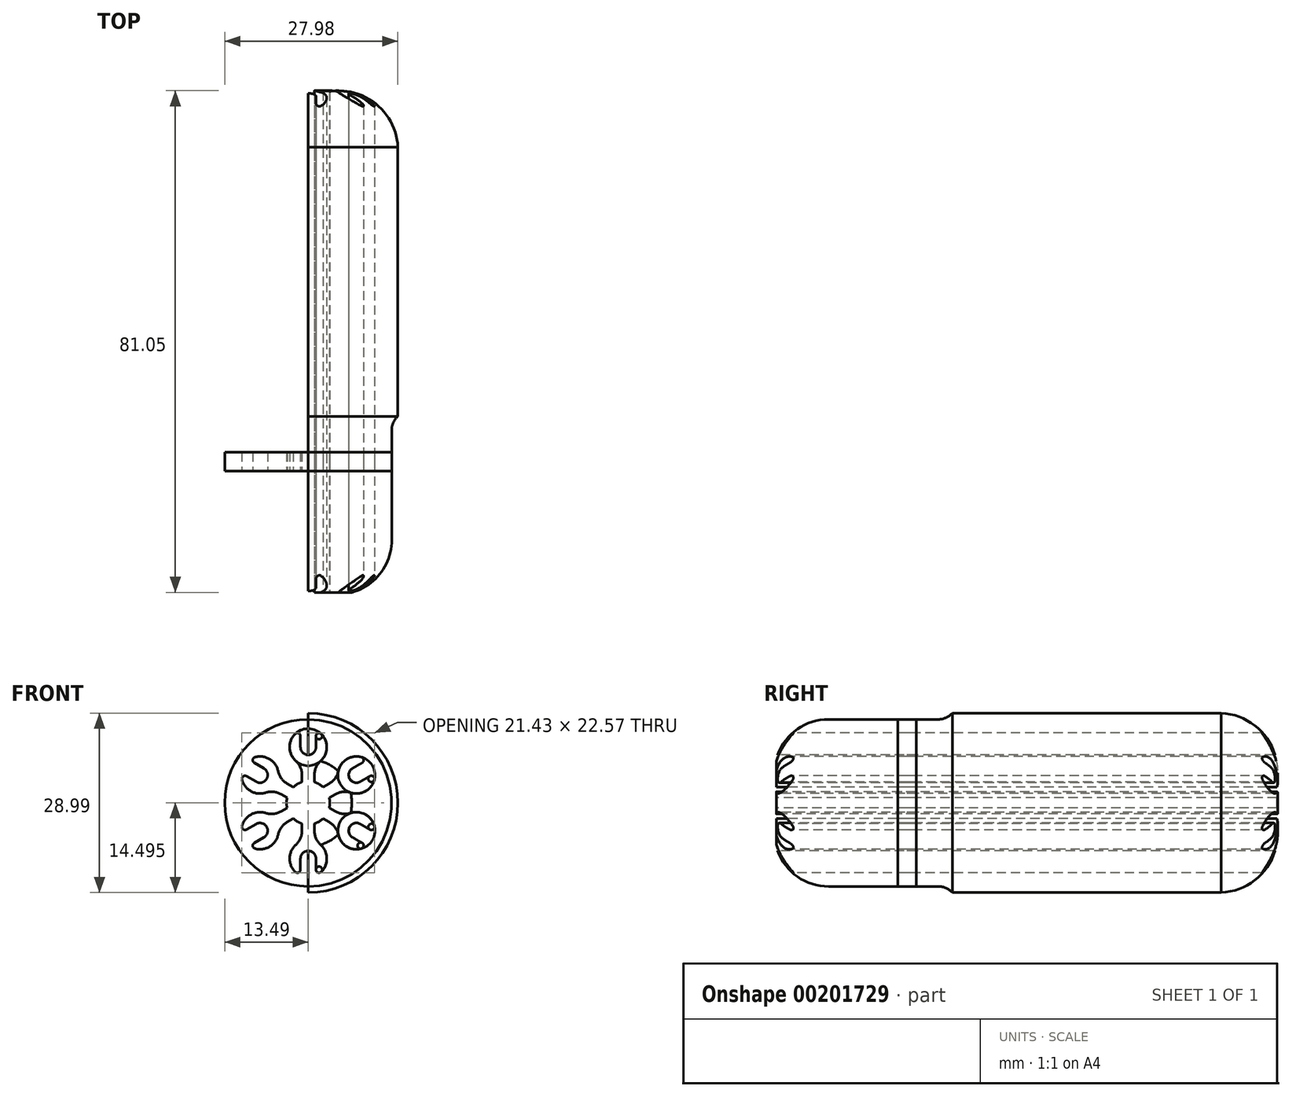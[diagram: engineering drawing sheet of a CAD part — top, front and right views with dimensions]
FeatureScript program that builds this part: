
annotation { "Feature Type Name" : "Feature", "Feature Type Description" : "" }
export const myFeature = defineFeature(function(context is Context, id is Id, definition is map)
    precondition{}
    {
        {
            var Q0;
            Q0=qCreatedBy(makeId("Right.planeOp"),FACE);
            var sketch = newSketch(context, id + "F0", { "sketchPlane" : qUnion([Q0])});
            skLineSegment(sketch, "E0.bottom", {"start": v(-3.13, 33.38) * mm, "end": v(86.87, 33.38) * mm});
            skLineSegment(sketch, "E0.top", {"start": v(-3.13, 32.38) * mm, "end": v(4.08, 32.38) * mm});
            skLineSegment(sketch, "E0.left", {"start": v(-3.13, 33.38) * mm, "end": v(-3.13, 32.38) * mm});
            skLineSegment(sketch, "E0.right", {"start": v(86.87, 33.38) * mm, "end": v(86.87, 32.38) * mm});
            skPoint(sketch, "E0.middle", {"position": v(41.87, 32.88) * mm});
            skLineSegment(sketch, "E1.bottom", {"start": v(86.87, 32.38) * mm, "end": v(81.87, 32.38) * mm, "construction": true});
            skLineSegment(sketch, "E1.top", {"start": v(86.87, 21.38) * mm, "end": v(85.87, 21.38) * mm});
            skLineSegment(sketch, "E1.left", {"start": v(86.87, 32.38) * mm, "end": v(86.87, 21.38) * mm, "construction": true});
            skLineSegment(sketch, "E1.right", {"start": v(81.87, 32.38) * mm, "end": v(81.87, 21.38) * mm, "construction": true});
            skLineSegment(sketch, "E2.bottom", {"start": v(81.87, 32.38) * mm, "end": v(71.87, 32.38) * mm, "construction": true});
            skLineSegment(sketch, "E2.top", {"start": v(81.87, 21.38) * mm, "end": v(71.87, 21.38) * mm, "construction": true});
            skLineSegment(sketch, "E2.right", {"start": v(71.87, 33.38) * mm, "end": v(71.87, 21.38) * mm, "construction": true});
            skLineSegment(sketch, "E3.0", {"start": v(85.87, 22.38) * mm, "end": v(85.37, 22.38) * mm, "construction": true});
            skLineSegment(sketch, "E4.0", {"start": v(85.87, 32.38) * mm, "end": v(85.87, 21.38) * mm, "construction": true});
            skArc(sketch, "E5", {"start": v(82.3, 22.38) * mm, "mid": v(80.84, 28.3) * mm, "end": v(76.33, 32.38) * mm});
            skArc(sketch, "E6", {"start": v(81.87, 21.38) * mm, "mid": v(79.3, 29.1) * mm, "end": v(71.87, 32.38) * mm});
            skLineSegment(sketch, "E7.trimOffspring", {"start": v(76.33, 32.38) * mm, "end": v(86.87, 32.38) * mm});
            skLineSegment(sketch, "E8.top", {"start": v(86.87, 25.38) * mm, "end": v(85.87, 25.38) * mm});
            skLineSegment(sketch, "E8.left", {"start": v(86.87, 23.38) * mm, "end": v(86.87, 25.38) * mm});
            skLineSegment(sketch, "E8.right", {"start": v(85.87, 22.38) * mm, "end": v(85.87, 22.72) * mm, "construction": true});
            skLineSegment(sketch, "E9.bottom", {"start": v(-3.13, 32.38) * mm, "end": v(-2.13, 32.38) * mm, "construction": true});
            skLineSegment(sketch, "E9.top", {"start": v(-3.13, 21.38) * mm, "end": v(-2.13, 21.38) * mm});
            skLineSegment(sketch, "E9.left", {"start": v(-3.13, 32.38) * mm, "end": v(-3.13, 21.38) * mm, "construction": true});
            skLineSegment(sketch, "E9.right", {"start": v(-2.13, 32.38) * mm, "end": v(-2.13, 21.38) * mm, "construction": true});
            skLineSegment(sketch, "E10.bottom", {"start": v(-2.13, 32.38) * mm, "end": v(4.08, 32.38) * mm, "construction": true});
            skLineSegment(sketch, "E10.top", {"start": v(-2.13, 33.38) * mm, "end": v(8.87, 33.38) * mm, "construction": true});
            skLineSegment(sketch, "E10.left", {"start": v(-2.13, 32.38) * mm, "end": v(-2.13, 33.38) * mm, "construction": true});
            skLineSegment(sketch, "E10.right", {"start": v(8.87, 32.38) * mm, "end": v(8.87, 33.38) * mm, "construction": true});
            skArc(sketch, "E11", {"start": v(4.08, 32.38) * mm, "mid": v(-1.17, 27.96) * mm, "end": v(-3.13, 21.38) * mm});
            skArc(sketch, "E12", {"start": v(8.87, 32.38) * mm, "mid": v(1.1, 29.16) * mm, "end": v(-2.13, 21.38) * mm});
            skLineSegment(sketch, "E13.trimOffspring", {"start": v(8.87, 32.38) * mm, "end": v(71.87, 32.38) * mm});
            skLineSegment(sketch, "E14", {"start": v(8.87, 21.38) * mm, "end": v(71.87, 21.38) * mm, "construction": true});
            skLineSegment(sketch, "E15.0", {"start": v(8.87, 17.38) * mm, "end": v(71.87, 17.38) * mm, "construction": true});
            skLineSegment(sketch, "E16.0", {"start": v(86.87, 23.38) * mm, "end": v(85.87, 23.38) * mm, "construction": true});
            skLineSegment(sketch, "E17.0", {"start": v(83.87, 21.38) * mm, "end": v(83.87, 25.38) * mm, "construction": true});
            skLineSegment(sketch, "E18", {"start": v(86.87, 23.38) * mm, "end": v(83.87, 21.38) * mm});
            skLineSegment(sketch, "E19.0", {"start": v(85.87, 23.92) * mm, "end": v(83.57, 22.38) * mm});
            skLineSegment(sketch, "E20.trimOffspring", {"start": v(83.87, 21.38) * mm, "end": v(81.87, 21.38) * mm});
            skLineSegment(sketch, "E21.trimOffspring", {"start": v(83.57, 22.38) * mm, "end": v(82.3, 22.38) * mm});
            skLineSegment(sketch, "E22.trimOffspring", {"start": v(85.87, 23.92) * mm, "end": v(85.87, 25.38) * mm});
            skLineSegment(sketch, "E23.bottom", {"start": v(8.87, 17.38) * mm, "end": v(-3.13, 17.38) * mm, "construction": true});
            skLineSegment(sketch, "E23.top", {"start": v(8.87, 21.38) * mm, "end": v(-3.13, 21.38) * mm, "construction": true});
            skLineSegment(sketch, "E23.left", {"start": v(8.87, 17.38) * mm, "end": v(8.87, 21.38) * mm, "construction": true});
            skLineSegment(sketch, "E23.right", {"start": v(-3.13, 17.38) * mm, "end": v(-3.13, 21.38) * mm, "construction": true});
            skSolve(sketch);
        }
        {
            var Q0;
            Q0=qCreatedBy(makeId("Right.planeOp"),FACE);
            var sketch = newSketch(context, id + "F1", { "sketchPlane" : qUnion([Q0])});
            skLineSegment(sketch, "E24.bottom", {"start": v(-3.13, 33.38) * mm, "end": v(28.58, 33.38) * mm, "construction": true});
            skLineSegment(sketch, "E24.left", {"start": v(-3.13, 33.38) * mm, "end": v(-3.13, 23.38) * mm, "construction": true});
            skLineSegment(sketch, "E24.right", {"start": v(28.58, 33.38) * mm, "end": v(28.58, 33.38) * mm});
            skLineSegment(sketch, "E25", {"start": v(28.58, 32.38) * mm, "end": v(8.84, 32.38) * mm, "construction": true});
            skArc(sketch, "E26", {"start": v(8.84, 32.38) * mm, "mid": v(1.84, 29.83) * mm, "end": v(-1.88, 23.38) * mm, "construction": true});
            skLineSegment(sketch, "E27.0", {"start": v(27.9, 31.88) * mm, "end": v(8.84, 31.88) * mm});
            skArc(sketch, "E28.0", {"start": v(8.84, 31.88) * mm, "mid": v(2.16, 29.45) * mm, "end": v(-1.38, 23.3) * mm});
            skLineSegment(sketch, "E29.0", {"start": v(26.58, 31.38) * mm, "end": v(8.84, 31.38) * mm});
            skArc(sketch, "E30.0", {"start": v(8.84, 30.88) * mm, "mid": v(2.9, 28.77) * mm, "end": v(-0.35, 23.38) * mm, "construction": true});
            skPoint(sketch, "E31.newPointB", {"position": v(28.58, 23.38) * mm});
            skArc(sketch, "E31.filletArc", {"start": v(26.58, 31.38) * mm, "mid": v(27.3, 31.5) * mm, "end": v(27.9, 31.88) * mm});
            skArc(sketch, "E32", {"start": v(8.84, 31.38) * mm, "mid": v(2.64, 29.01) * mm, "end": v(-0.4, 23.12) * mm});
            skLineSegment(sketch, "E33.trimOffspring", {"start": v(-1.37, 23.38) * mm, "end": v(-0.35, 23.38) * mm});
            skSolve(sketch);
        }
        {
            var Q0;
            Q0=qCreatedBy(makeId("Right.planeOp"),FACE);
            var sketch = newSketch(context, id + "F2", { "sketchPlane" : qUnion([Q0])});
            skLineSegment(sketch, "E34", {"start": v(86.87, 23.38) * mm, "end": v(83.87, 21.38) * mm, "construction": true});
            skLineSegment(sketch, "E35", {"start": v(83.87, 21.38) * mm, "end": v(81.87, 21.38) * mm, "construction": true});
            skLineSegment(sketch, "E36.0", {"start": v(86.87, 22.78) * mm, "end": v(84.02, 20.88) * mm});
            skLineSegment(sketch, "E37.0", {"start": v(84.02, 20.88) * mm, "end": v(81.87, 20.88) * mm});
            skLineSegment(sketch, "E38", {"start": v(86.87, 22.78) * mm, "end": v(86.87, 17.38) * mm});
            skLineSegment(sketch, "E39.0", {"start": v(66.87, 20.38) * mm, "end": v(66.87, 17.38) * mm});
            skLineSegment(sketch, "E40.0", {"start": v(81.87, 20.38) * mm, "end": v(66.87, 20.38) * mm});
            skLineSegment(sketch, "E41", {"start": v(71.87, 17.38) * mm, "end": v(66.87, 17.38) * mm});
            skLineSegment(sketch, "E42", {"start": v(71.87, 17.38) * mm, "end": v(86.87, 17.38) * mm});
            skLineSegment(sketch, "E43.0", {"start": v(81.87, 20.88) * mm, "end": v(81.87, 20.38) * mm});
            skSolve(sketch);
        }
        {
            var Q0;
            Q0=qCreatedBy(makeId("Right.planeOp"),FACE);
            var sketch = newSketch(context, id + "F3", { "sketchPlane" : qUnion([Q0])});
            skArc(sketch, "E44", {"start": v(81.87, 21.38) * mm, "mid": v(79.3, 29.1) * mm, "end": v(71.87, 32.38) * mm, "construction": true});
            skArc(sketch, "E45.0", {"start": v(81.3, 20.88) * mm, "mid": v(79.25, 28.4) * mm, "end": v(72.28, 31.88) * mm});
            skLineSegment(sketch, "E46", {"start": v(81.87, 20.38) * mm, "end": v(69.18, 20.38) * mm, "construction": true});
            skLineSegment(sketch, "E47", {"start": v(28.58, 32.38) * mm, "end": v(37.05, 32.38) * mm});
            skLineSegment(sketch, "E48", {"start": v(26.58, 31.38) * mm, "end": v(22.5, 31.38) * mm});
            skArc(sketch, "E49", {"start": v(26.58, 31.38) * mm, "mid": v(27.7, 31.64) * mm, "end": v(28.58, 32.38) * mm});
            skLineSegment(sketch, "E50.0", {"start": v(28.58, 31.88) * mm, "end": v(72.28, 31.88) * mm});
            skArc(sketch, "E51.0", {"start": v(26.58, 30.88) * mm, "mid": v(27.93, 31.2) * mm, "end": v(28.98, 32.08) * mm});
            skLineSegment(sketch, "E52.0", {"start": v(26.58, 30.88) * mm, "end": v(8.74, 30.88) * mm});
            skLineSegment(sketch, "E53.0", {"start": v(81.3, 20.88) * mm, "end": v(0.37, 20.88) * mm});
            skArc(sketch, "E54", {"start": v(8.84, 31.38) * mm, "mid": v(2.74, 29.11) * mm, "end": v(-0.35, 23.38) * mm, "construction": true});
            skArc(sketch, "E55.0", {"start": v(8.83, 30.88) * mm, "mid": v(3.5, 29.1) * mm, "end": v(0.37, 24.44) * mm});
            skLineSegment(sketch, "E56", {"start": v(-2.13, 27.58) * mm, "end": v(-2.13, 15.19) * mm, "construction": true});
            skLineSegment(sketch, "E57.trimOffspring", {"start": v(0.37, 24.44) * mm, "end": v(0.37, 20.88) * mm});
            skSolve(sketch);
        }
        {
            var Q0;
            Q0=qSketchRegion(id+"F3",true);
            var Q1;
            Q1=sQuery(id+"F0.wireOp",EDGE,"E15.0");
            revolve(context, id + "F4", {"entities" : qUnion([Q0]), "axis" : qUnion([Q1]), "revolveType" : RevolveType.ONE_DIRECTION, "angle" : 180 * degree});
        }
        {
            var Q0;
            Q0=qCreatedBy(makeId("Front.planeOp"),FACE);
            var sketch = newSketch(context, id + "F5", { "sketchPlane" : qUnion([Q0])});
            skCircle(sketch, "E58", {"center": v(0, 17.38) * mm, "radius": 14.5 * mm, "construction": true});
            skCircle(sketch, "E59", {"center": v(0, 17.38) * mm, "radius": 3.5 * mm});
            skLineSegment(sketch, "E60", {"start": v(0, 17.38) * mm, "end": v(0, 5.38) * mm, "construction": true});
            skPoint(sketch, "E61", {"position": v(0, 5.38) * mm});
            skPoint(sketch, "E62", {"position": v(-16.26, 26.77) * mm});
            skLineSegment(sketch, "E63.0", {"start": v(-1, 14.03) * mm, "end": v(-1, 12.86) * mm});
            skLineSegment(sketch, "E64.0", {"start": v(1, 14.03) * mm, "end": v(1, 12.86) * mm});
            skArc(sketch, "E65", {"start": v(-2, 10.62) * mm, "mid": v(-3, 8.45) * mm, "end": v(-2.1, 6.24) * mm});
            skPoint(sketch, "E66.visualSharp", {"position": v(-1, 11.21) * mm});
            skArc(sketch, "E66.filletArc", {"start": v(-2, 10.62) * mm, "mid": v(-1.26, 11.63) * mm, "end": v(-1, 12.86) * mm});
            skPoint(sketch, "E67.visualSharp", {"position": v(1, 11.21) * mm});
            skArc(sketch, "E67.filletArc", {"start": v(1, 12.86) * mm, "mid": v(1.26, 11.63) * mm, "end": v(2, 10.62) * mm});
            skArc(sketch, "E68", {"start": v(1.25, 8.38) * mm, "mid": v(0, 9.63) * mm, "end": v(-1.25, 8.38) * mm});
            skLineSegment(sketch, "E69", {"start": v(1.25, 8.38) * mm, "end": v(1.25, 6.6) * mm});
            skLineSegment(sketch, "E70", {"start": v(0, 8.38) * mm, "end": v(-1.25, 8.38) * mm, "construction": true});
            skLineSegment(sketch, "E71", {"start": v(-1.25, 8.38) * mm, "end": v(-1.25, 6.6) * mm});
            skArc(sketch, "E72.trimOffspring", {"start": v(2.1, 6.24) * mm, "mid": v(3, 8.45) * mm, "end": v(2, 10.62) * mm});
            skPoint(sketch, "E73.visualSharp", {"position": v(-1.25, 5.66) * mm});
            skArc(sketch, "E73.filletArc", {"start": v(-2.1, 6.24) * mm, "mid": v(-1.56, 6.14) * mm, "end": v(-1.25, 6.6) * mm});
            skPoint(sketch, "E74.visualSharp", {"position": v(1.25, 5.66) * mm});
            skArc(sketch, "E74.filletArc", {"start": v(1.25, 6.6) * mm, "mid": v(1.56, 6.14) * mm, "end": v(2.1, 6.24) * mm});
            skSolve(sketch);
        }
        {
            var Q0;
            {var subQ0=sQuery(id+"F5.wireOp",EDGE,"E63.0");Q0=makeQuery(id+"F5.imprint","IMPRINT",FACE,{"disambiguationData":[TD([[makeQuery(id+"F5.imprint","IMPRINT",EDGE,{"derivedFrom":subQ0}),1.0]])]});}
            extrude(context, id + "F6", {"entities" : qUnion([Q0]), "oppositeDirection" : true, "depth" : 90 * mm});
        }
        {
            var Q0;
            Q0=qCreatedBy(makeId("Right.planeOp"),FACE);
            var sketch = newSketch(context, id + "F7", { "sketchPlane" : qUnion([Q0])});
            skLineSegment(sketch, "E75", {"start": v(0, 17.38) * mm, "end": v(41.07, 17.38) * mm});
            skSolve(sketch);
        }
        {
            var Q0;
            Q0=makeQuery(id+"F6.opExtrude","SWEPT_BODY",BODY,{"disambiguationData":[OSD([sQuery(id+"F5.wireOp",EDGE,"E59"),sQuery(id+"F5.wireOp",EDGE,"E63.0"),sQuery(id+"F5.wireOp",EDGE,"E64.0"),sQuery(id+"F5.wireOp",EDGE,"E65")])]});
            var Q1;
            Q1=sQuery(id+"F7.wireOp",EDGE,"E75");
            circularPattern(context, id + "F8", {"entities" : qUnion([Q0]), "axis" : qUnion([Q1]), "angle" : 360 * degree, "instanceCount" : 6, "equalSpace" : true});
        }
        {
            var Q0;
            Q0=makeQuery(id+"F6.opExtrude","SWEPT_BODY",BODY,{"disambiguationData":[OSD([sQuery(id+"F5.wireOp",EDGE,"E59"),sQuery(id+"F5.wireOp",EDGE,"E63.0"),sQuery(id+"F5.wireOp",EDGE,"E64.0"),sQuery(id+"F5.wireOp",EDGE,"E65"),sQuery(id+"F5.wireOp",EDGE,"E66.filletArc"),sQuery(id+"F5.wireOp",EDGE,"E67.filletArc"),sQuery(id+"F5.wireOp",EDGE,"E68"),sQuery(id+"F5.wireOp",EDGE,"E69"),sQuery(id+"F5.wireOp",EDGE,"E71"),sQuery(id+"F5.wireOp",EDGE,"E72.trimOffspring"),sQuery(id+"F5.wireOp",EDGE,"E73.filletArc"),sQuery(id+"F5.wireOp",EDGE,"E74.filletArc")])]});
            var Q1;
            Q1=makeQuery(id+"F8.opPattern","COPY",BODY,{"derivedFrom":makeQuery(id+"F6.opExtrude","SWEPT_BODY",BODY,{"disambiguationData":[OSD([sQuery(id+"F5.wireOp",EDGE,"E59"),sQuery(id+"F5.wireOp",EDGE,"E63.0"),sQuery(id+"F5.wireOp",EDGE,"E64.0"),sQuery(id+"F5.wireOp",EDGE,"E65"),sQuery(id+"F5.wireOp",EDGE,"E66.filletArc"),sQuery(id+"F5.wireOp",EDGE,"E67.filletArc"),sQuery(id+"F5.wireOp",EDGE,"E68"),sQuery(id+"F5.wireOp",EDGE,"E69"),sQuery(id+"F5.wireOp",EDGE,"E71"),sQuery(id+"F5.wireOp",EDGE,"E72.trimOffspring"),sQuery(id+"F5.wireOp",EDGE,"E73.filletArc"),sQuery(id+"F5.wireOp",EDGE,"E74.filletArc")])]}),"instanceName":"5"});
            var Q2;
            Q2=makeQuery(id+"F8.opPattern","COPY",BODY,{"derivedFrom":makeQuery(id+"F6.opExtrude","SWEPT_BODY",BODY,{"disambiguationData":[OSD([sQuery(id+"F5.wireOp",EDGE,"E59"),sQuery(id+"F5.wireOp",EDGE,"E63.0"),sQuery(id+"F5.wireOp",EDGE,"E64.0"),sQuery(id+"F5.wireOp",EDGE,"E65"),sQuery(id+"F5.wireOp",EDGE,"E66.filletArc"),sQuery(id+"F5.wireOp",EDGE,"E67.filletArc"),sQuery(id+"F5.wireOp",EDGE,"E68"),sQuery(id+"F5.wireOp",EDGE,"E69"),sQuery(id+"F5.wireOp",EDGE,"E71"),sQuery(id+"F5.wireOp",EDGE,"E72.trimOffspring"),sQuery(id+"F5.wireOp",EDGE,"E73.filletArc"),sQuery(id+"F5.wireOp",EDGE,"E74.filletArc")])]}),"instanceName":"4"});
            var Q3;
            Q3=makeQuery(id+"F8.opPattern","COPY",BODY,{"derivedFrom":makeQuery(id+"F6.opExtrude","SWEPT_BODY",BODY,{"disambiguationData":[OSD([sQuery(id+"F5.wireOp",EDGE,"E59"),sQuery(id+"F5.wireOp",EDGE,"E63.0"),sQuery(id+"F5.wireOp",EDGE,"E64.0"),sQuery(id+"F5.wireOp",EDGE,"E65"),sQuery(id+"F5.wireOp",EDGE,"E66.filletArc"),sQuery(id+"F5.wireOp",EDGE,"E67.filletArc"),sQuery(id+"F5.wireOp",EDGE,"E68"),sQuery(id+"F5.wireOp",EDGE,"E69"),sQuery(id+"F5.wireOp",EDGE,"E71"),sQuery(id+"F5.wireOp",EDGE,"E72.trimOffspring"),sQuery(id+"F5.wireOp",EDGE,"E73.filletArc"),sQuery(id+"F5.wireOp",EDGE,"E74.filletArc")])]}),"instanceName":"3"});
            var Q4;
            Q4=makeQuery(id+"F4.opRevolve","SWEPT_BODY",BODY,{"disambiguationData":[OSD([sQuery(id+"F3.wireOp",EDGE,"E45.0"),sQuery(id+"F3.wireOp",EDGE,"E50.0"),sQuery(id+"F3.wireOp",EDGE,"E51.0"),sQuery(id+"F3.wireOp",EDGE,"E52.0"),sQuery(id+"F3.wireOp",EDGE,"E53.0"),sQuery(id+"F3.wireOp",EDGE,"E55.0"),sQuery(id+"F3.wireOp",EDGE,"E57.trimOffspring")])]});
            booleanBodies(context, id + "F9", {"operationType" : BooleanOperationType.SUBTRACTION, "tools" : qUnion([Q0, Q1, Q2, Q3]), "targets" : qUnion([Q4]), "keepTools" : true});
        }
        {
            var Q0;
            Q0 = qSketchRegion(id + "F3", true);
            var Q1;
            Q1=sQuery(id+"F0.wireOp",EDGE,"E15.0");
            revolve(context, id + "F10", {"entities" : qUnion([Q0]), "axis" : qUnion([Q1]), "revolveType" : RevolveType.FULL});
        }
        {
            var Q0;
            Q0=qCreatedBy(makeId("Front.planeOp"),FACE);
            var sketch = newSketch(context, id + "F11", { "sketchPlane" : qUnion([Q0])});
            skCircle(sketch, "E76.0", {"center": v(0, 17.38) * mm, "radius": 13.5 * mm});
            skSolve(sketch);
        }
        {
            var Q0;
            Q0 = qSketchRegion(id + "F11", true);
            extrude(context, id + "F12", {"entities" : qUnion([Q0]), "oppositeDirection" : true, "depth" : 23 * mm, "hasSecondDirection" : true, "secondDirectionOppositeDirection" : true, "secondDirectionDepth" : 20 * mm});
        }
        {
            var Q0;
            Q0=makeQuery(id+"F6.opExtrude","SWEPT_BODY",BODY,{"disambiguationData":[OSD([sQuery(id+"F5.wireOp",EDGE,"E59"),sQuery(id+"F5.wireOp",EDGE,"E63.0"),sQuery(id+"F5.wireOp",EDGE,"E64.0"),sQuery(id+"F5.wireOp",EDGE,"E65"),sQuery(id+"F5.wireOp",EDGE,"E66.filletArc"),sQuery(id+"F5.wireOp",EDGE,"E67.filletArc"),sQuery(id+"F5.wireOp",EDGE,"E68"),sQuery(id+"F5.wireOp",EDGE,"E69"),sQuery(id+"F5.wireOp",EDGE,"E71"),sQuery(id+"F5.wireOp",EDGE,"E72.trimOffspring"),sQuery(id+"F5.wireOp",EDGE,"E73.filletArc"),sQuery(id+"F5.wireOp",EDGE,"E74.filletArc")])]});
            var Q1;
            Q1=makeQuery(id+"F8.opPattern","COPY",BODY,{"derivedFrom":makeQuery(id+"F6.opExtrude","SWEPT_BODY",BODY,{"disambiguationData":[OSD([sQuery(id+"F5.wireOp",EDGE,"E59"),sQuery(id+"F5.wireOp",EDGE,"E63.0"),sQuery(id+"F5.wireOp",EDGE,"E64.0"),sQuery(id+"F5.wireOp",EDGE,"E65"),sQuery(id+"F5.wireOp",EDGE,"E66.filletArc"),sQuery(id+"F5.wireOp",EDGE,"E67.filletArc"),sQuery(id+"F5.wireOp",EDGE,"E68"),sQuery(id+"F5.wireOp",EDGE,"E69"),sQuery(id+"F5.wireOp",EDGE,"E71"),sQuery(id+"F5.wireOp",EDGE,"E72.trimOffspring"),sQuery(id+"F5.wireOp",EDGE,"E73.filletArc"),sQuery(id+"F5.wireOp",EDGE,"E74.filletArc")])]}),"instanceName":"5"});
            var Q2;
            Q2=makeQuery(id+"F8.opPattern","COPY",BODY,{"derivedFrom":makeQuery(id+"F6.opExtrude","SWEPT_BODY",BODY,{"disambiguationData":[OSD([sQuery(id+"F5.wireOp",EDGE,"E59"),sQuery(id+"F5.wireOp",EDGE,"E63.0"),sQuery(id+"F5.wireOp",EDGE,"E64.0"),sQuery(id+"F5.wireOp",EDGE,"E65"),sQuery(id+"F5.wireOp",EDGE,"E66.filletArc"),sQuery(id+"F5.wireOp",EDGE,"E67.filletArc"),sQuery(id+"F5.wireOp",EDGE,"E68"),sQuery(id+"F5.wireOp",EDGE,"E69"),sQuery(id+"F5.wireOp",EDGE,"E71"),sQuery(id+"F5.wireOp",EDGE,"E72.trimOffspring"),sQuery(id+"F5.wireOp",EDGE,"E73.filletArc"),sQuery(id+"F5.wireOp",EDGE,"E74.filletArc")])]}),"instanceName":"4"});
            var Q3;
            Q3=makeQuery(id+"F8.opPattern","COPY",BODY,{"derivedFrom":makeQuery(id+"F6.opExtrude","SWEPT_BODY",BODY,{"disambiguationData":[OSD([sQuery(id+"F5.wireOp",EDGE,"E59"),sQuery(id+"F5.wireOp",EDGE,"E63.0"),sQuery(id+"F5.wireOp",EDGE,"E64.0"),sQuery(id+"F5.wireOp",EDGE,"E65"),sQuery(id+"F5.wireOp",EDGE,"E66.filletArc"),sQuery(id+"F5.wireOp",EDGE,"E67.filletArc"),sQuery(id+"F5.wireOp",EDGE,"E68"),sQuery(id+"F5.wireOp",EDGE,"E69"),sQuery(id+"F5.wireOp",EDGE,"E71"),sQuery(id+"F5.wireOp",EDGE,"E72.trimOffspring"),sQuery(id+"F5.wireOp",EDGE,"E73.filletArc"),sQuery(id+"F5.wireOp",EDGE,"E74.filletArc")])]}),"instanceName":"3"});
            var Q4;
            Q4=makeQuery(id+"F8.opPattern","COPY",BODY,{"derivedFrom":makeQuery(id+"F6.opExtrude","SWEPT_BODY",BODY,{"disambiguationData":[OSD([sQuery(id+"F5.wireOp",EDGE,"E59"),sQuery(id+"F5.wireOp",EDGE,"E63.0"),sQuery(id+"F5.wireOp",EDGE,"E64.0"),sQuery(id+"F5.wireOp",EDGE,"E65"),sQuery(id+"F5.wireOp",EDGE,"E66.filletArc"),sQuery(id+"F5.wireOp",EDGE,"E67.filletArc"),sQuery(id+"F5.wireOp",EDGE,"E68"),sQuery(id+"F5.wireOp",EDGE,"E69"),sQuery(id+"F5.wireOp",EDGE,"E71"),sQuery(id+"F5.wireOp",EDGE,"E72.trimOffspring"),sQuery(id+"F5.wireOp",EDGE,"E73.filletArc"),sQuery(id+"F5.wireOp",EDGE,"E74.filletArc")])]}),"instanceName":"2"});
            var Q5;
            Q5=makeQuery(id+"F8.opPattern","COPY",BODY,{"derivedFrom":makeQuery(id+"F6.opExtrude","SWEPT_BODY",BODY,{"disambiguationData":[OSD([sQuery(id+"F5.wireOp",EDGE,"E59"),sQuery(id+"F5.wireOp",EDGE,"E63.0"),sQuery(id+"F5.wireOp",EDGE,"E64.0"),sQuery(id+"F5.wireOp",EDGE,"E65"),sQuery(id+"F5.wireOp",EDGE,"E66.filletArc"),sQuery(id+"F5.wireOp",EDGE,"E67.filletArc"),sQuery(id+"F5.wireOp",EDGE,"E68"),sQuery(id+"F5.wireOp",EDGE,"E69"),sQuery(id+"F5.wireOp",EDGE,"E71"),sQuery(id+"F5.wireOp",EDGE,"E72.trimOffspring"),sQuery(id+"F5.wireOp",EDGE,"E73.filletArc"),sQuery(id+"F5.wireOp",EDGE,"E74.filletArc")])]}),"instanceName":"1"});
            var Q6;
            Q6=makeQuery(id+"F10.opRevolve","SWEPT_BODY",BODY,{"disambiguationData":[OSD([sQuery(id+"F3.wireOp",EDGE,"E45.0"),sQuery(id+"F3.wireOp",EDGE,"E50.0"),sQuery(id+"F3.wireOp",EDGE,"E51.0"),sQuery(id+"F3.wireOp",EDGE,"E52.0"),sQuery(id+"F3.wireOp",EDGE,"E53.0"),sQuery(id+"F3.wireOp",EDGE,"E55.0"),sQuery(id+"F3.wireOp",EDGE,"E57.trimOffspring")])]});
            booleanBodies(context, id + "F13", {"operationType" : BooleanOperationType.SUBTRACTION, "tools" : qUnion([Q0, Q1, Q2, Q3, Q4, Q5]), "targets" : qUnion([Q6])});
        }
        {
            var Q0;
            Q0=makeQuery(id+"F10.opRevolve","SWEPT_BODY",BODY,{"disambiguationData":[OSD([sQuery(id+"F3.wireOp",EDGE,"E45.0"),sQuery(id+"F3.wireOp",EDGE,"E50.0"),sQuery(id+"F3.wireOp",EDGE,"E51.0"),sQuery(id+"F3.wireOp",EDGE,"E52.0"),sQuery(id+"F3.wireOp",EDGE,"E53.0"),sQuery(id+"F3.wireOp",EDGE,"E55.0"),sQuery(id+"F3.wireOp",EDGE,"E57.trimOffspring")])]});
            var Q1;
            Q1=makeQuery(id+"F12.opExtrude","SWEPT_BODY",BODY,{"disambiguationData":[OSD([sQuery(id+"F11.wireOp",EDGE,"E76.0")])]});
            booleanBodies(context, id + "F14", {"operationType" : BooleanOperationType.INTERSECTION, "tools" : qUnion([Q0, Q1])});
        }
    });
